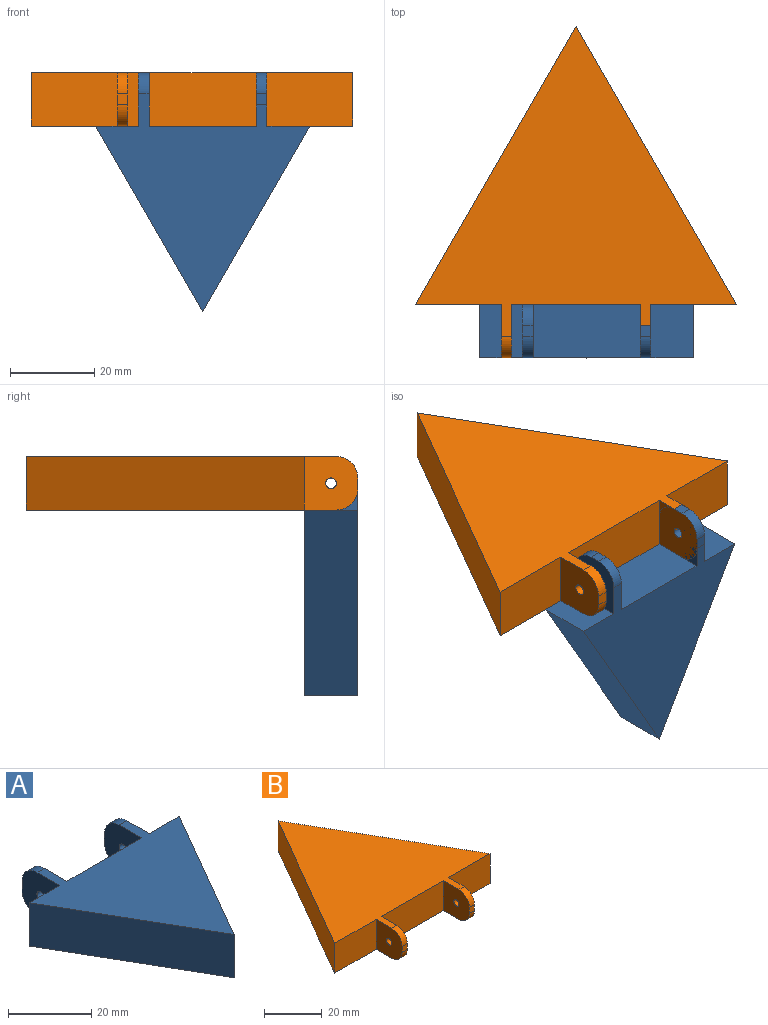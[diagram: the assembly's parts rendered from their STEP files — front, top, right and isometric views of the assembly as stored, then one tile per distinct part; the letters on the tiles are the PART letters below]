
ASSEMBLY  parts=2 mates=1
PART A: 19 faces, bbox 50.8x56.7x12.7 mm
  f0: plane 12.7x10.16mm, normal (0,1,0), area 129mm2, adj f4,f5,f6,f10
  f1: plane 25.4x12.7mm, normal (0,1,0), area 322.6mm2, adj f5,f6,f8,f11
  f2: plane 43.99x25.4mm, normal (0.87,-0.5,0), area 645.2mm2, adj f3,f4,f5,f6
  f3: plane 12.7x10.16mm, normal (0,1,0), area 129mm2, adj f2,f5,f6,f7
  f4: plane 43.99x25.4mm, normal (-0.87,-0.5,0), area 645.2mm2, adj f0,f2,f5,f6
  f5: plane 51.61x50.8mm, normal (0,0,1), area 1156.2mm2, adj f0,f1,f2,f3,f4,f7,f8,f10
  f6: plane 51.61x50.8mm, normal (0,0,-1), area 1156.2mm2, adj f0,f1,f2,f3,f4,f7,f8,f10
  f7: plane 12.7x12.7mm, normal (1,0,0), area 145.1mm2, adj f3,f5,f6,f9,f13,f15,f16
  f8: plane 12.7x12.7mm, normal (-1,0,0), area 145.1mm2, adj f1,f5,f6,f9,f13,f15,f16
  f9: plane 2.54x2.54mm, normal (0,1,0), area 6.5mm2, adj f7,f8,f15,f16
  f10: plane 12.7x12.7mm, normal (-1,0,0), area 145.1mm2, adj f0,f5,f6,f12,f14,f17,f18
  f11: plane 12.7x12.7mm, normal (1,0,0), area 145.1mm2, adj f1,f5,f6,f12,f14,f17,f18
  f12: plane 2.54x2.54mm, normal (0,1,0), area 6.5mm2, adj f10,f11,f17,f18
  f13: cylinder r=1.27mm len=2.54mm, axis (1,0,0), area 20.3mm2, adj f7,f8
  f14: cylinder r=1.27mm len=2.54mm, axis (-1,0,0), area 20.3mm2, adj f10,f11
  f15: cylinder r=5.08mm len=5.08mm, axis (-1,0,0), area 20.3mm2, adj f6,f7,f8,f9
  f16: cylinder r=5.08mm len=5.08mm, axis (1,0,0), area 20.3mm2, adj f5,f7,f8,f9
  f17: cylinder r=5.08mm len=5.08mm, axis (1,0,0), area 20.3mm2, adj f5,f10,f11,f12
  f18: cylinder r=5.08mm len=5.08mm, axis (-1,0,0), area 20.3mm2, adj f6,f10,f11,f12
PART B: 19 faces, bbox 76.2x78.7x12.7 mm
  f0: plane 20.32x12.7mm, normal (0,-1,0), area 258.1mm2, adj f2,f5,f6,f10
  f1: plane 30.48x12.7mm, normal (0,-1,0), area 387.1mm2, adj f5,f6,f8,f11
  f2: plane 65.99x38.1mm, normal (0.87,0.5,0), area 967.7mm2, adj f0,f3,f5,f6
  f3: plane 65.99x38.1mm, normal (-0.87,0.5,0), area 967.7mm2, adj f2,f4,f5,f6
  f4: plane 20.32x12.7mm, normal (0,-1,0), area 258.1mm2, adj f3,f5,f6,f7
  f5: plane 76.2x73.61mm, normal (0,0,1), area 2553mm2, adj f0,f1,f2,f3,f4,f7,f8,f10
  f6: plane 76.2x73.61mm, normal (0,0,-1), area 2553mm2, adj f0,f1,f2,f3,f4,f7,f8,f10
  f7: plane 12.7x12.7mm, normal (-1,0,0), area 145.1mm2, adj f4,f5,f6,f9,f14,f17,f18
  f8: plane 12.7x12.7mm, normal (1,0,0), area 145.1mm2, adj f1,f5,f6,f9,f14,f17,f18
  f9: plane 2.54x2.54mm, normal (0,-1,0), area 6.5mm2, adj f7,f8,f17,f18
  f10: plane 12.7x12.7mm, normal (1,0,0), area 145.1mm2, adj f0,f5,f6,f12,f13,f15,f16
  f11: plane 12.7x12.7mm, normal (-1,0,0), area 145.1mm2, adj f1,f5,f6,f12,f13,f15,f16
  f12: plane 2.54x2.54mm, normal (0,-1,0), area 6.5mm2, adj f10,f11,f15,f16
  f13: cylinder r=1.27mm len=2.54mm, axis (1,0,0), area 20.3mm2, adj f10,f11
  f14: cylinder r=1.27mm len=2.54mm, axis (-1,0,0), area 20.3mm2, adj f7,f8
  f15: cylinder r=5.08mm len=5.08mm, axis (-1,0,0), area 20.3mm2, adj f5,f10,f11,f12
  f16: cylinder r=5.08mm len=5.08mm, axis (1,0,0), area 20.3mm2, adj f6,f10,f11,f12
  f17: cylinder r=5.08mm len=5.08mm, axis (1,0,0), area 20.3mm2, adj f6,f7,f8,f9
  f18: cylinder r=5.08mm len=5.08mm, axis (-1,0,0), area 20.3mm2, adj f5,f7,f8,f9
PLACE A rot(axis=(1,0,0),90deg) t=(-5.16,-27.31,-15.34)mm
PLACE B t=(-7.7,-5.31,-0.67)mm
MATE revolute A.f14 <-> B.f14  axis (1,0,0) through (10.08,-33.66,5.68)mm
